# Revit family: FAP62T-UL2043
name_source: partatom
category: Communication Devices
revit_build: Autodesk Revit 2014 (Build: 20140709_2115(x64)
units: mm (PartAtom-declared; Revit-internal decimal feet)

## types (1)
- Two Way, Full Range, Coaxial Ceiling Loudspeaker
    100V Taps = 2, 4, 8, 16, and 32 Watts  & 8Q Bypass. Primary taps (@70.7V)
    70V Taps = 2, 4, 8, 16, and 32 Watts  & 8Ω
    Baffle Material = <By Category>
    Body Material = QF_Metal - Stainless - Polished
    Color = <By Category>
    Controls = Front Mounted Tap Selector Switch.
    Cost = 0 $
    Cost MSRP = 0 $
    Coverage = Add coverage view
    Coverage Horizontal = 110.00°
    Coverage Vertical = 110.00°
    Depth = 12.5 "
    Description = 6" COAXIAL IN-CEILING LOUDSPEAKER WITH 32-WATT 70/100V TRANSFORMER, PORTED ENCLOSURE, AND UL2043 CERTIFICATION
    Dispersion Angle = 110.00°
    Enclosure Material = <By Category>
    Extended Low Frequency Response = 285 cubic Inch Optimally Tuned
    Family Code (default) = LOUD SPEAKERS
    Frequency Response  = 63Hz – 20kHz
    Grill Material = QF_Plastic - Black - Matte
    Height = 8.48 "
    IQ Category = SPEAKERS
    Impedance = 8
    Ingress Protection = IP-21
    Manufacturer = ATLAS SOUND
    Manufacturer URL = https://www.atlasied.com
    Market = Commercial, Higher Education, Emergency
    MasterFormat = 27 41 13
    MaterFormat Title = SPEAKERS
    Model = FAP62T-UL2043
    Mount Material = QF_Plastic - White - Smooth
    OmniClass Number = 23-37 17 13 19
    OmniClass Title = SPEAKERS
    Power Rating (RMS) = 50 Watts
    Product Page URL = https://www.atlasied.com
    Regulatory Compliance = UL Listed to Comply with UL1480, UL2043 and CSA60065. Suitable for Use in Air Handling Spaces per NFPA 70 and NFPA 90
    SPL Max = 107
    Safety Agency Ratings = UL Listed to Comply with UL1480, UL2043 and CSA60065. Suitable for Use in Air Handling Spaces per NFPA 70 and NFPA 90
    ScheduleType |RF| = AtlasIED Master
    Sensitivity = 88
    Speaker Dispersion = 110.00°
    Speaker Type = S1
    Transformer Option = Yes
    URL = www.atlassound.com
    Vertical Symmetry = Yes
    Warranty = 5 Year
    Width = 12.5 "

## geometry (parser evidence)
native form markers: Blend x6, Sweep x2
no freeform markers — native parametric forms only
